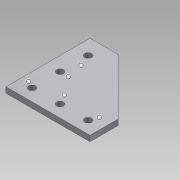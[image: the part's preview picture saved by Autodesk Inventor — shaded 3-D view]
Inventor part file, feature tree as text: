
AUTODESK INVENTOR PART (.ipt)
format: ipt  version: 2013 SP2 (Build 170200200, 200)  size: 93,184 bytes
history: native  units: mm
features: sketch x1, extrude x1, hole x1
ambient origin geometry x8: Origin, YZ Plane, XZ Plane, XY Plane, X Axis, Y Axis, Z Axis, Center Point
bodies: Solid1 (feature_tree)
feature tree (3):
  sketch  "Sketch1"  dims[d0=60.0mm d1=90.0deg d2=20.0mm d3=135.0deg d4=60.0mm d5=20.0mm d6=10.0mm d7=20.0mm d8=20.0mm d9=20.0mm d10=20.0mm d11=4.0mm d12=0.0mm d13=5.0mm d14=6.0mm d15=4.0mm d16=2.0mm d17=90.0deg d18=8.0mm d19=20.594885mm d38=0.0mm d39=0.0mm d40=0.0mm d41=0.0mm d42=0.0mm d43=0.0mm d44=0.0mm d45=0.0mm d48=0.0mm d49=0.0mm]
  extrude  "Extrusion1"  TaperAngle=90.0deg  [1 undecoded]
  hole  "Hole1"  [1 undecoded]
note: 2 required parameter values undecoded (feature->parameter linkage not recoverable at this tier; creation-order binding heuristic only, values carry confidence <= 0.55)
